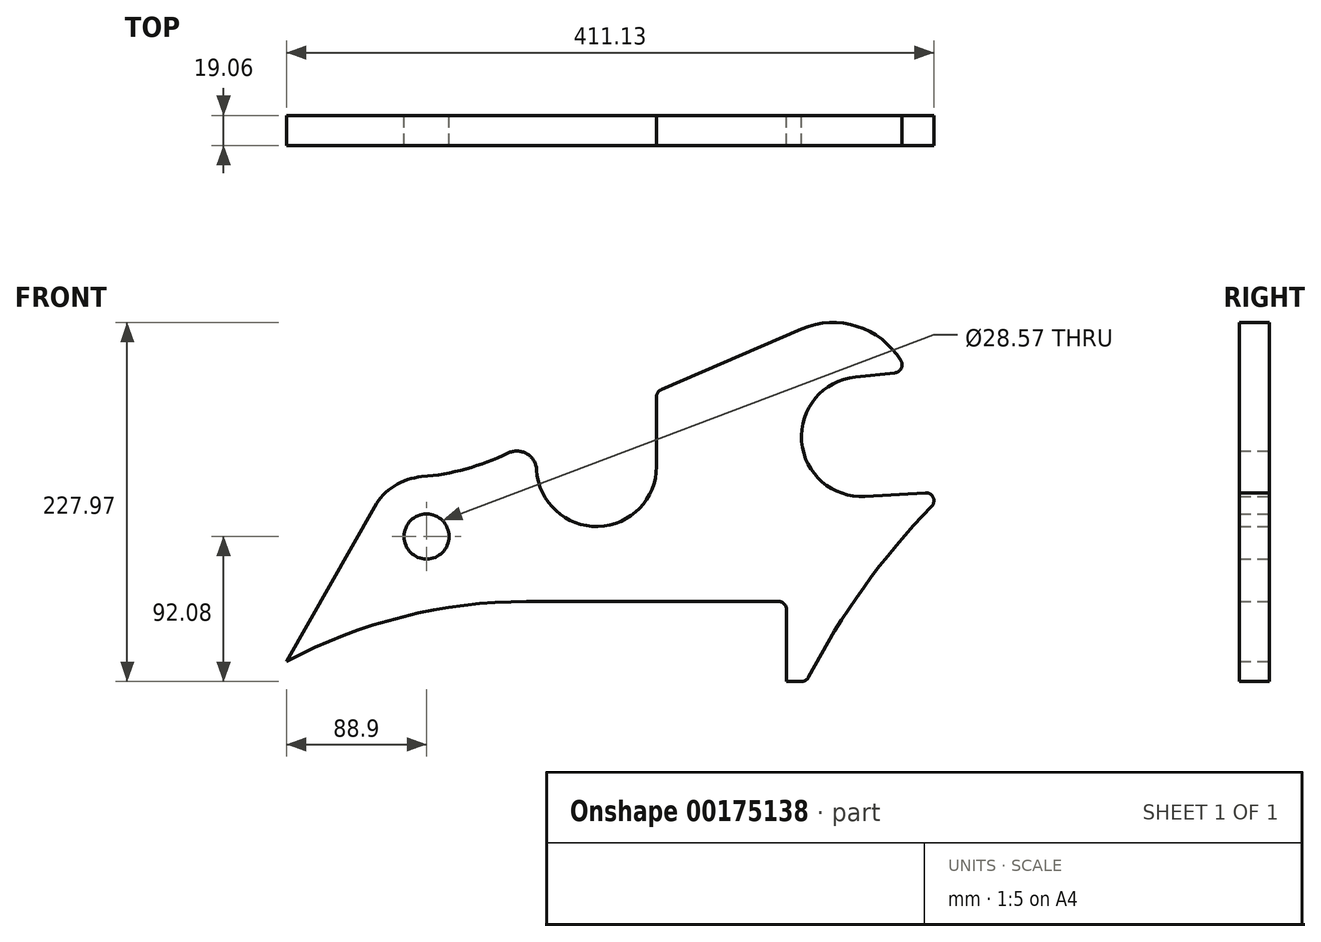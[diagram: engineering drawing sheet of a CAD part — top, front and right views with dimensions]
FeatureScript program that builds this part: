
annotation { "Feature Type Name" : "Feature", "Feature Type Description" : "" }
export const myFeature = defineFeature(function(context is Context, id is Id, definition is map)
    precondition{}
    {
        {
            var Q0;
            Q0=qCreatedBy(makeId("Front.planeOp"),FACE);
            var sketch = newSketch(context, id + "F0", { "sketchPlane" : qUnion([Q0])});
            skLineSegment(sketch, "E0.bottom", {"start": v(-279.4, -146.05) * mm, "end": v(273.05, -146.05) * mm, "construction": true});
            skLineSegment(sketch, "E0.top", {"start": v(-279.4, 228.6) * mm, "end": v(273.05, 228.6) * mm, "construction": true});
            skLineSegment(sketch, "E0.left", {"start": v(-279.4, -146.05) * mm, "end": v(-279.4, 228.6) * mm, "construction": true});
            skLineSegment(sketch, "E0.right", {"start": v(273.05, -146.05) * mm, "end": v(273.05, 228.6) * mm, "construction": true});
            skCircle(sketch, "E1", {"center": v(-107.95, -44.45) * mm, "radius": 14.29 * mm});
            skArc(sketch, "E2", {"start": v(-38.04, -2.16) * mm, "mid": v(1.08, -38.08) * mm, "end": v(38.1, 0) * mm});
            skArc(sketch, "E3", {"start": v(164.34, 56.95) * mm, "mid": v(130.3, 15.94) * mm, "end": v(170.56, -18.98) * mm});
            skLineSegment(sketch, "E4", {"start": v(-215.9, -146.05) * mm, "end": v(-215.9, 228.6) * mm, "construction": true});
            skPoint(sketch, "E5", {"position": v(-196.85, -123.83) * mm});
            skPoint(sketch, "E6", {"position": v(-38.1, 19.05) * mm});
            skPoint(sketch, "E7", {"position": v(38.1, 47.63) * mm});
            skPoint(sketch, "E8", {"position": v(130.17, 87.31) * mm});
            skPoint(sketch, "E9", {"position": v(196.85, 60.33) * mm});
            skPoint(sketch, "E10", {"position": v(133.35, -136.52) * mm});
            skArc(sketch, "E11", {"start": v(-111.01, -6.47) * mm, "mid": v(-128.43, -12.32) * mm, "end": v(-141.08, -25.63) * mm});
            skLineSegment(sketch, "E12", {"start": v(-196.85, -123.83) * mm, "end": v(-141.08, -25.63) * mm});
            skArc(sketch, "E13", {"start": v(-38.04, -2.16) * mm, "mid": v(-44.3, 8.09) * mm, "end": v(-56.3, 8.53) * mm});
            skLineSegment(sketch, "E14", {"start": v(38.1, 47.63) * mm, "end": v(38.1, 0) * mm});
            skLineSegment(sketch, "E15", {"start": v(38.1, 47.62) * mm, "end": v(130.17, 87.31) * mm});
            skArc(sketch, "E16", {"start": v(196.85, 60.33) * mm, "mid": v(169.15, 87.75) * mm, "end": v(130.17, 87.31) * mm});
            skLineSegment(sketch, "E17", {"start": v(196.85, 60.33) * mm, "end": v(164.34, 56.95) * mm});
            skLineSegment(sketch, "E18", {"start": v(170.56, -18.98) * mm, "end": v(222.25, -15.87) * mm});
            skArc(sketch, "E19", {"start": v(222.25, -15.87) * mm, "mid": v(172.82, -72.53) * mm, "end": v(133.35, -136.53) * mm});
            skLineSegment(sketch, "E20", {"start": v(133.35, -136.52) * mm, "end": v(120.65, -136.52) * mm});
            skLineSegment(sketch, "E21", {"start": v(120.65, -136.52) * mm, "end": v(120.65, -85.72) * mm});
            skLineSegment(sketch, "E22", {"start": v(120.65, -85.72) * mm, "end": v(-44.45, -85.72) * mm});
            skArc(sketch, "E23", {"start": v(-44.45, -85.72) * mm, "mid": v(-123, -95.4) * mm, "end": v(-196.85, -123.82) * mm});
            skArc(sketch, "E24", {"start": v(-111.01, -6.47) * mm, "mid": v(-82.95, -1.54) * mm, "end": v(-56.3, 8.53) * mm});
            skSolve(sketch);
        }
        {
            var Q0;
            Q0=qSketchRegion(id+"F0",true);
            extrude(context, id + "F1", {"entities" : qUnion([Q0]), "endBound" : BoundingType.SYMMETRIC, "depth" : 19.05 * mm});
        }
        {
            var Q0;
            Q0=makeQuery(id+"F1.opExtrude","SWEPT_EDGE",EDGE,{"disambiguationData":[OSD([sQuery(id+"F0.wireOp",EDGE,"E14"),sQuery(id+"F0.wireOp",EDGE,"E15")])]});
            var Q1;
            Q1=makeQuery(id+"F1.opExtrude","SWEPT_EDGE",EDGE,{"disambiguationData":[OSD([sQuery(id+"F0.wireOp",EDGE,"E16"),sQuery(id+"F0.wireOp",EDGE,"E17")])]});
            var Q2;
            Q2=makeQuery(id+"F1.opExtrude","SWEPT_EDGE",EDGE,{"disambiguationData":[OSD([sQuery(id+"F0.wireOp",EDGE,"E18"),sQuery(id+"F0.wireOp",EDGE,"E19")])]});
            var Q3;
            Q3=makeQuery(id+"F1.opExtrude","SWEPT_EDGE",EDGE,{"disambiguationData":[OSD([sQuery(id+"F0.wireOp",EDGE,"E19"),sQuery(id+"F0.wireOp",EDGE,"E20")])]});
            var Q4;
            Q4=makeQuery(id+"F1.opExtrude","SWEPT_EDGE",EDGE,{"disambiguationData":[OSD([sQuery(id+"F0.wireOp",EDGE,"E21"),sQuery(id+"F0.wireOp",EDGE,"E22")])]});
            fillet(context, id + "F2", {"entities" : qUnion([Q0, Q1, Q2, Q3, Q4]), "radius" : 5.08 * mm, "tangentPropagation" : true, "allowEdgeOverflow" : false});
        }
    });
